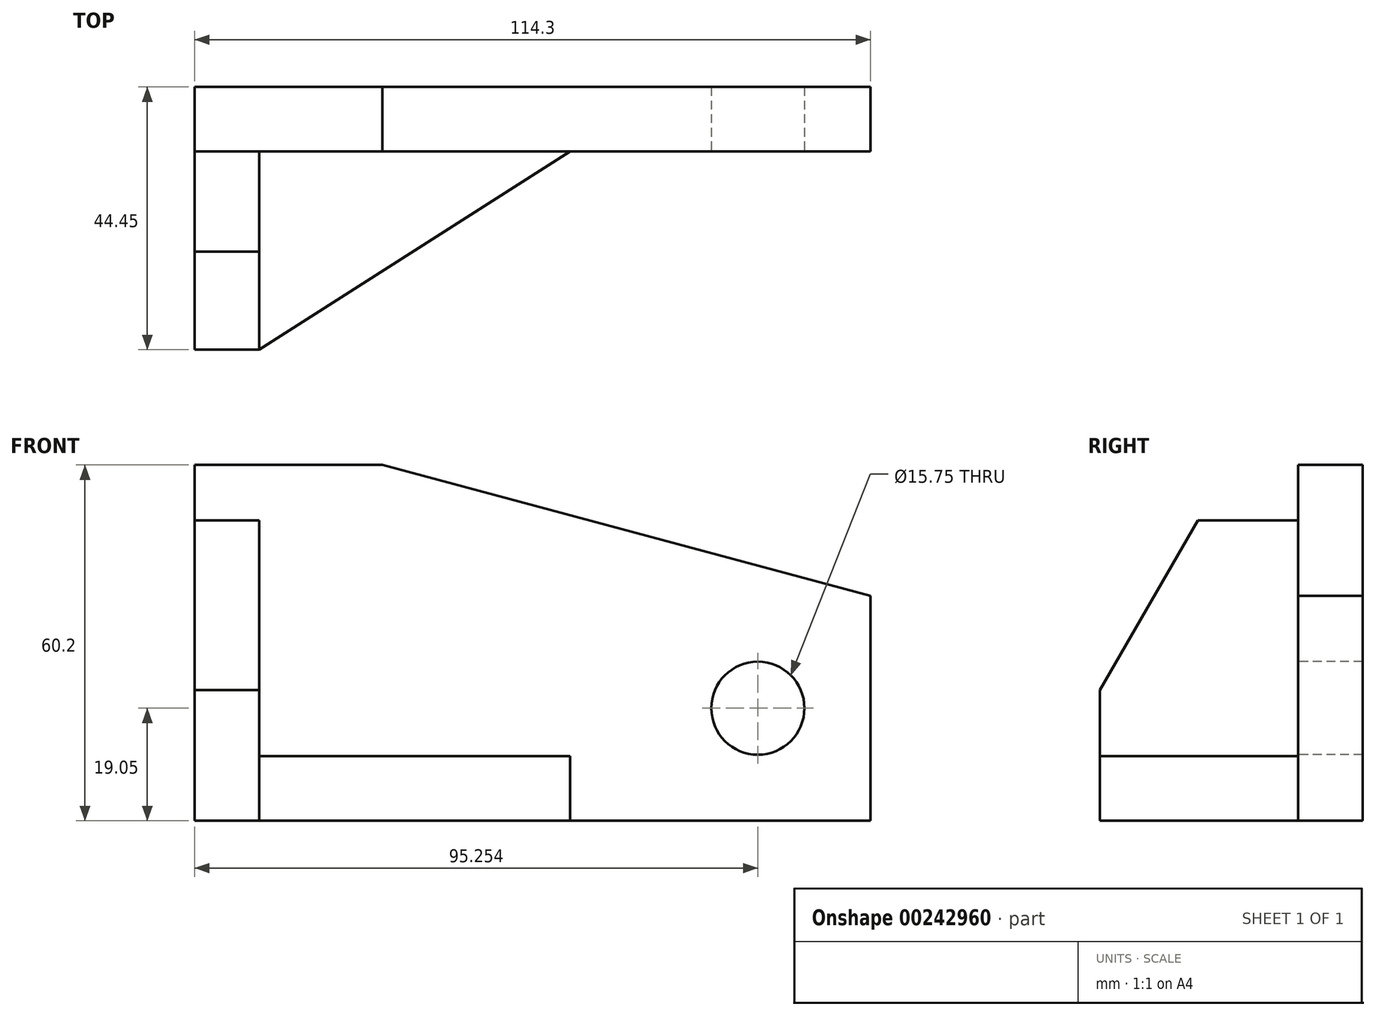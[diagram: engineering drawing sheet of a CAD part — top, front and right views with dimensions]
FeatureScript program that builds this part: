
annotation { "Feature Type Name" : "Feature", "Feature Type Description" : "" }
export const myFeature = defineFeature(function(context is Context, id is Id, definition is map)
    precondition{}
    {
        {
            var Q0;
            Q0=qCreatedBy(makeId("Top.planeOp"),FACE);
            var sketch = newSketch(context, id + "F0", { "sketchPlane" : qUnion([Q0])});
            skLineSegment(sketch, "E0.bottom", {"start": v(-54.54, -14.26) * mm, "end": v(59.76, -14.26) * mm});
            skLineSegment(sketch, "E0.top", {"start": v(-54.54, -25.19) * mm, "end": v(59.76, -25.19) * mm});
            skLineSegment(sketch, "E0.left", {"start": v(-54.54, -14.26) * mm, "end": v(-54.54, -25.19) * mm});
            skLineSegment(sketch, "E0.right", {"start": v(59.76, -14.26) * mm, "end": v(59.76, -25.19) * mm});
            skLineSegment(sketch, "E1.top", {"start": v(-54.54, -58.71) * mm, "end": v(-43.61, -58.71) * mm});
            skLineSegment(sketch, "E1.left", {"start": v(-54.54, -25.19) * mm, "end": v(-54.54, -58.71) * mm});
            skLineSegment(sketch, "E1.right", {"start": v(-43.61, -25.19) * mm, "end": v(-43.61, -58.71) * mm});
            skLineSegment(sketch, "E2", {"start": v(-43.61, -58.71) * mm, "end": v(8.96, -25.19) * mm});
            skLineSegment(sketch, "E3", {"start": v(-22.79, -14.26) * mm, "end": v(-22.79, -25.19) * mm});
            skSolve(sketch);
        }
        {
            var Q0;
            {var subQ0=sQuery(id+"F0.wireOp",EDGE,"E1.right");Q0=makeQuery(id+"F0.imprint","IMPRINT",FACE,{"disambiguationData":[TD([[makeQuery(id+"F0.imprint","IMPRINT",EDGE,{"derivedFrom":subQ0}),1.0]])]});}
            extrude(context, id + "F1", {"entities" : qUnion([Q0]), "depth" : 10.92 * mm});
        }
        {
            var Q0;
            Q0=makeQuery(id+"F0.imprint","IMPRINT",FACE,{"disambiguationData":[TD([[makeQuery(id+"F0.imprint","IMPRINT",EDGE,{"derivedFrom":sQuery(id+"F0.wireOp",EDGE,"E0.left")}),1.0]])]});
            var Q1;
            Q1=makeQuery(id+"F0.imprint","IMPRINT",FACE,{"disambiguationData":[TD([[makeQuery(id+"F0.imprint","IMPRINT",EDGE,{"derivedFrom":sQuery(id+"F0.wireOp",EDGE,"E0.bottom")}),-1.0]])]});
            extrude(context, id + "F2", {"entities" : qUnion([Q0, Q1]), "operationType" : NewBodyOperationType.ADD, "depth" : 60.2 * mm});
        }
        {
            var Q0;
            Q0=makeQuery(id+"F0.imprint","IMPRINT",FACE,{"disambiguationData":[TD([[makeQuery(id+"F0.imprint","IMPRINT",EDGE,{"derivedFrom":sQuery(id+"F0.wireOp",EDGE,"E1.top")}),1.0]])]});
            extrude(context, id + "F3", {"entities" : qUnion([Q0]), "operationType" : NewBodyOperationType.ADD, "depth" : 50.8 * mm});
        }
        {
            var Q0;
            Q0=makeQuery(id+"F2.opExtrude","SWEPT_FACE",FACE,{"disambiguationData":[OSD([sQuery(id+"F0.wireOp",EDGE,"E0.top"),sQuery(id+"F0.wireOp",EDGE,"E1.bottom")])]});
            var sketch = newSketch(context, id + "F4", { "sketchPlane" : qUnion([Q0])});
            skCircle(sketch, "E4", {"center": v(40.71, 19.05) * mm, "radius": 7.87 * mm});
            skLineSegment(sketch, "E5", {"start": v(-54.54, 60.2) * mm, "end": v(-22.79, 60.2) * mm});
            skLineSegment(sketch, "E6", {"start": v(-22.79, 60.2) * mm, "end": v(59.76, 38.08) * mm});
            skSolve(sketch);
        }
        {
            var Q0;
            Q0=makeQuery(id+"F3.opExtrude","SWEPT_FACE",FACE,{"disambiguationData":[OSD([sQuery(id+"F0.wireOp",EDGE,"E1.right")])]});
            var sketch = newSketch(context, id + "F5", { "sketchPlane" : qUnion([Q0])});
            skLineSegment(sketch, "E7", {"start": v(-58.71, 22.1) * mm, "end": v(-42.14, 50.8) * mm});
            skSolve(sketch);
        }
        {
            var Q0;
            Q0=makeQuery(id+"F4.imprint","IMPRINT",FACE,{"disambiguationData":[TD([[makeQuery(id+"F4.imprint","IMPRINT",EDGE,{"derivedFrom":sQuery(id+"F4.wireOp",EDGE,"E4")}),1.0]])]});
            extrude(context, id + "F6", {"entities" : qUnion([Q0]), "operationType" : NewBodyOperationType.REMOVE, "oppositeDirection" : true, "depth" : 25.4 * mm});
        }
        {
            var Q0;
            {var subQ0=sQuery(id+"F5.wireOp",EDGE,"E7");var subQ1=sQuery(id+"F0.wireOp",EDGE,"E1.right");var subQ4=makeQuery(id+"F3.opExtrude","CAP_EDGE",EDGE,{"disambiguationData":[OSD([subQ1])],"isStart":false});var subQ5=makeQuery(id+"F5.imprint","INTERSECT",VERTEX,{"derivedFrom":[subQ4,subQ0]});Q0=makeQuery(id+"F5.imprint","IMPRINT",FACE,{"disambiguationData":[TD([[makeQuery(id+"F5.imprint","IMPRINT",EDGE,{"disambiguationData":[TD([[subQ5,1.0]])],"derivedFrom":subQ0}),1.0]])]});}
            extrude(context, id + "F7", {"entities" : qUnion([Q0]), "operationType" : NewBodyOperationType.REMOVE, "oppositeDirection" : true, "depth" : 25.4 * mm});
        }
        {
            var Q0;
            {var subQ0=sQuery(id+"F4.wireOp",EDGE,"E6");Q0=makeQuery(id+"F4.imprint","IMPRINT",FACE,{"disambiguationData":[TD([[makeQuery(id+"F4.imprint","IMPRINT",EDGE,{"derivedFrom":subQ0}),1.0]])]});}
            extrude(context, id + "F8", {"entities" : qUnion([Q0]), "operationType" : NewBodyOperationType.REMOVE, "endBound" : BoundingType.THROUGH_ALL, "oppositeDirection" : true, "depth" : 25.4 * mm});
        }
    });
